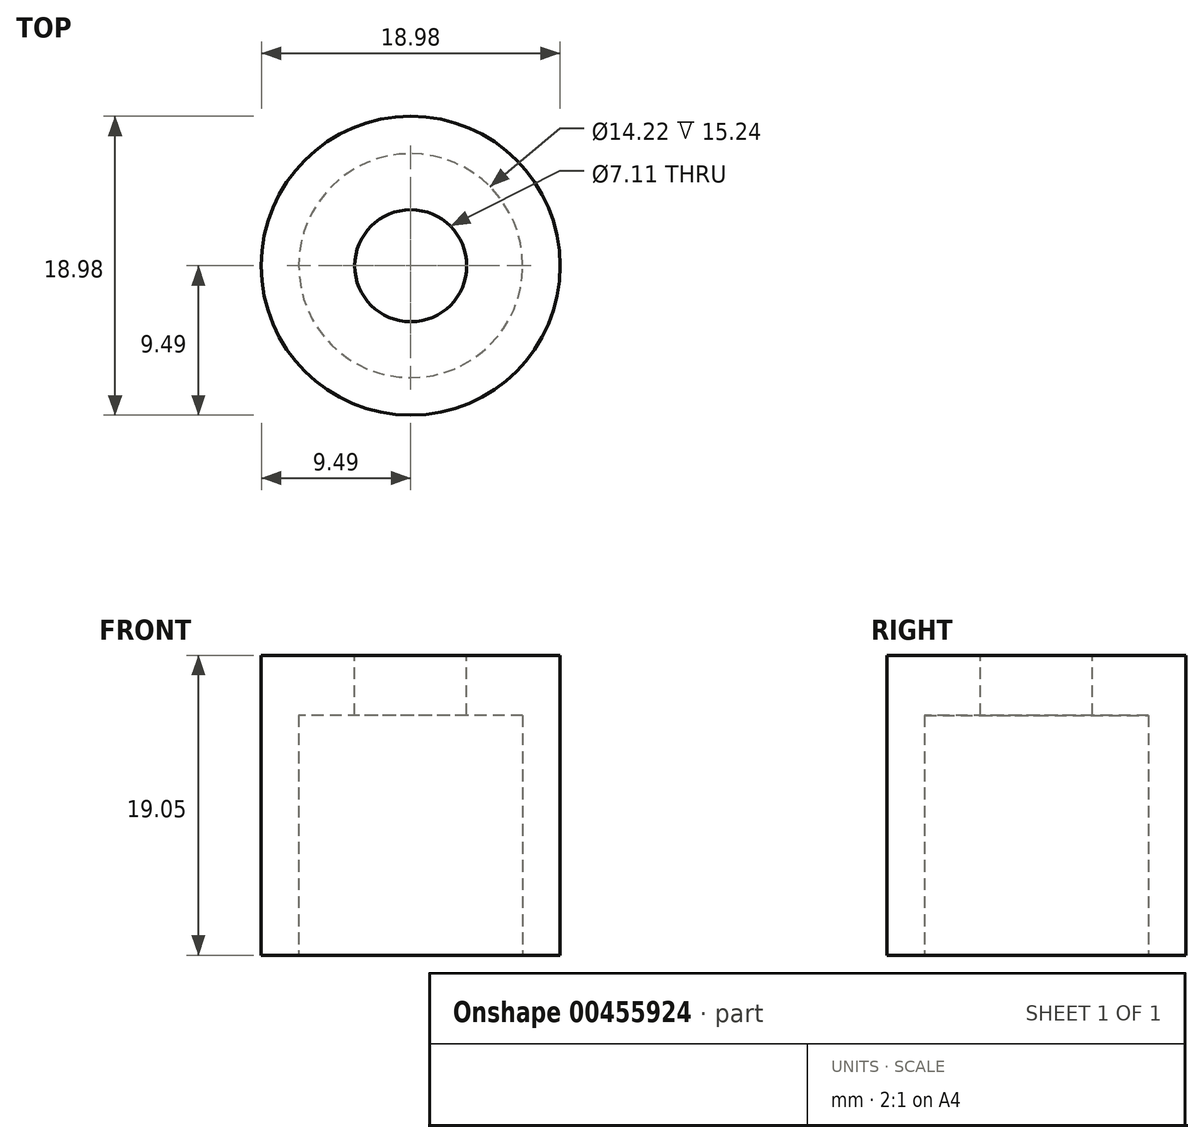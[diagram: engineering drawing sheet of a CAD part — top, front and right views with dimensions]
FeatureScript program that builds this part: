
annotation { "Feature Type Name" : "Feature", "Feature Type Description" : "" }
export const myFeature = defineFeature(function(context is Context, id is Id, definition is map)
    precondition{}
    {
        {
            var Q0;
            Q0=qCreatedBy(makeId("Top.planeOp"),FACE);
            var sketch = newSketch(context, id + "F0", { "sketchPlane" : qUnion([Q0])});
            skCircle(sketch, "E0", {"center": v(0, 0) * mm, "radius": 7.11 * mm});
            skCircle(sketch, "E1.0", {"center": v(0, 0) * mm, "radius": 9.5 * mm});
            skSolve(sketch);
        }
        {
            var Q0;
            Q0 = qSketchRegion(id + "F0", true);
            extrude(context, id + "F1", {"entities" : qUnion([Q0]), "depth" : 19.05 * mm, "offsetDistance" : 25.4 * mm});
        }
        {
            var Q0;
            Q0=makeQuery(id+"F1.opExtrude","CAP_FACE",FACE,{"disambiguationData":[OSD([sQuery(id+"F0.wireOp",EDGE,"E0"),sQuery(id+"F0.wireOp",EDGE,"E1.0")])],"isStart":false});
            var sketch = newSketch(context, id + "F2", { "sketchPlane" : qUnion([Q0])});
            skCircle(sketch, "E2", {"center": v(0, 0) * mm, "radius": 3.56 * mm});
            skSolve(sketch);
        }
        {
            var Q0;
            Q0=makeQuery(id+"F2.imprint","IMPRINT",FACE,{"disambiguationData":[TD([[makeQuery(id+"F2.imprint","IMPRINT",EDGE,{"derivedFrom":sQuery(id+"F2.wireOp",EDGE,"E2")}),-1.0]])]});
            extrude(context, id + "F3", {"entities" : qUnion([Q0]), "operationType" : NewBodyOperationType.ADD, "oppositeDirection" : true, "depth" : 3.8 * mm, "offsetDistance" : 25.4 * mm});
        }
    });
